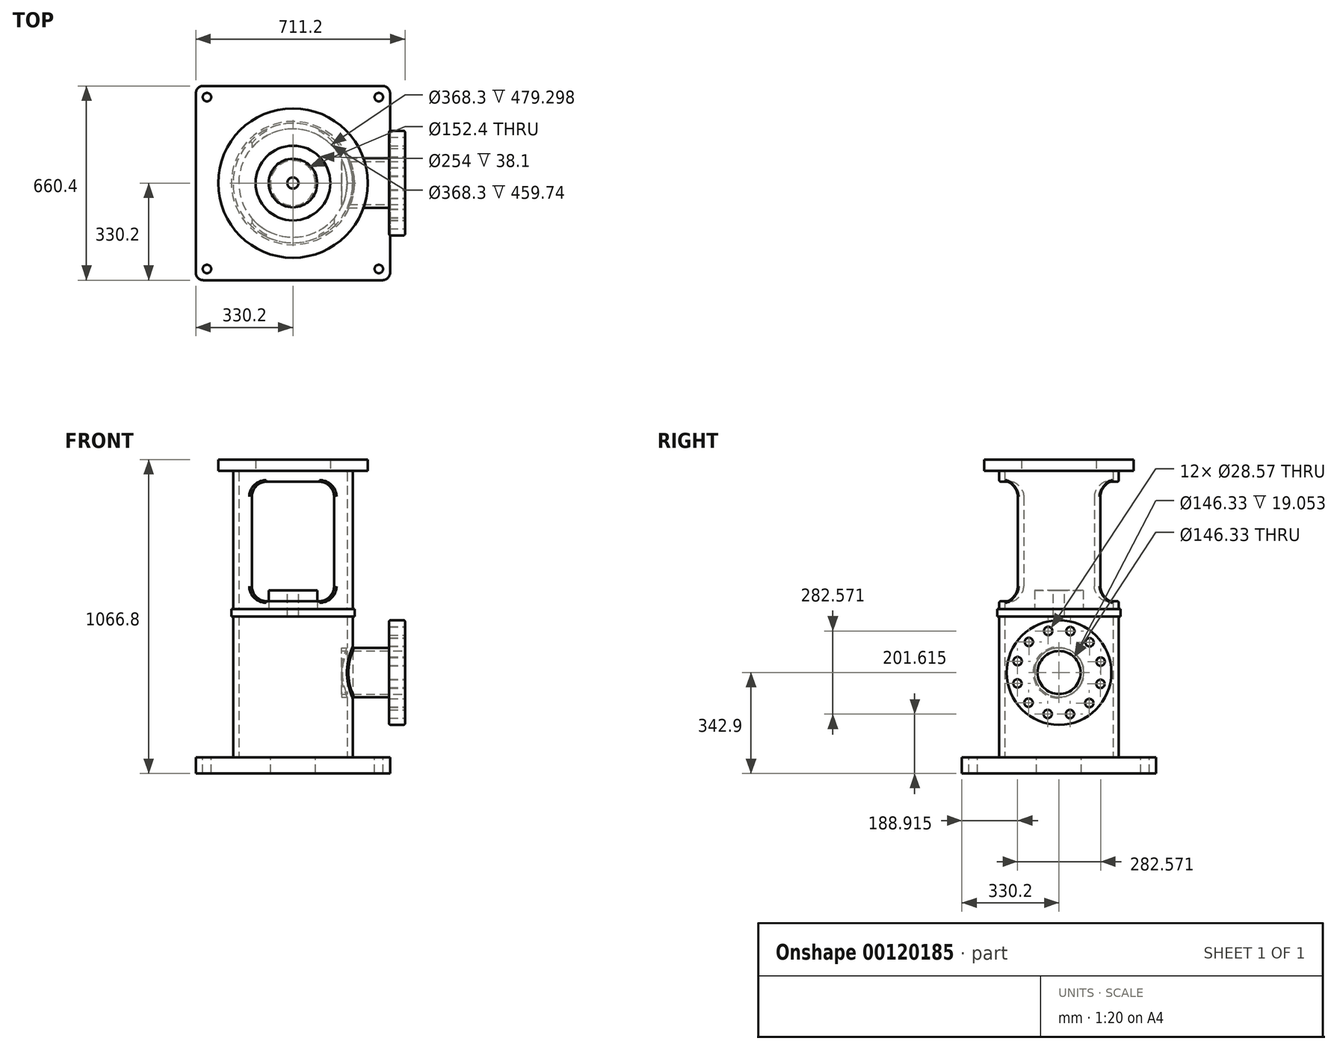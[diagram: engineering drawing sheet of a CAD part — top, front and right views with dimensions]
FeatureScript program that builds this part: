
annotation { "Feature Type Name" : "Feature", "Feature Type Description" : "" }
export const myFeature = defineFeature(function(context is Context, id is Id, definition is map)
    precondition{}
    {
        {
            var Q0;
            Q0=qCreatedBy(makeId("Top.planeOp"),FACE);
            var sketch = newSketch(context, id + "F0", { "sketchPlane" : qUnion([Q0])});
            skLineSegment(sketch, "E0.bottom", {"start": v(330.2, 330.2) * mm, "end": v(-330.2, 330.2) * mm});
            skLineSegment(sketch, "E0.top", {"start": v(330.2, -330.2) * mm, "end": v(-330.2, -330.2) * mm});
            skLineSegment(sketch, "E0.left", {"start": v(330.2, 330.2) * mm, "end": v(330.2, -330.2) * mm});
            skLineSegment(sketch, "E0.right", {"start": v(-330.2, 330.2) * mm, "end": v(-330.2, -330.2) * mm});
            skPoint(sketch, "E0.middle", {"position": v(0, 0) * mm});
            skSolve(sketch);
        }
        {
            var Q0;
            Q0 = qSketchRegion(id + "F0", true);
            extrude(context, id + "F1", {"entities" : qUnion([Q0]), "depth" : 54.1 * mm});
        }
        {
            var Q0;
            Q0=makeQuery(id+"F1.opExtrude","CAP_FACE",FACE,{"disambiguationData":[OSD([sQuery(id+"F0.wireOp",EDGE,"E0.bottom"),sQuery(id+"F0.wireOp",EDGE,"E0.top"),sQuery(id+"F0.wireOp",EDGE,"E0.left"),sQuery(id+"F0.wireOp",EDGE,"E0.right")])],"isStart":false});
            var sketch = newSketch(context, id + "F2", { "sketchPlane" : qUnion([Q0])});
            skCircle(sketch, "E1", {"center": v(0, 0) * mm, "radius": 203.2 * mm});
            skCircle(sketch, "E2", {"center": v(0, 0) * mm, "radius": 184.15 * mm});
            skSolve(sketch);
        }
        {
            var Q0;
            Q0 = qSketchRegion(id + "F2", true);
            extrude(context, id + "F3", {"entities" : qUnion([Q0]), "operationType" : NewBodyOperationType.ADD, "depth" : 974.6 * mm});
        }
        {
            var Q0;
            Q0=makeQuery(id+"F3.opExtrude","CAP_FACE",FACE,{"disambiguationData":[OSD([sQuery(id+"F2.wireOp",EDGE,"E1"),sQuery(id+"F2.wireOp",EDGE,"E2")])],"isStart":false});
            var sketch = newSketch(context, id + "F4", { "sketchPlane" : qUnion([Q0])});
            skCircle(sketch, "E3", {"center": v(0, 0) * mm, "radius": 127 * mm});
            skCircle(sketch, "E4", {"center": v(0, 0) * mm, "radius": 254 * mm});
            skSolve(sketch);
        }
        {
            var Q0;
            Q0 = qSketchRegion(id + "F4", true);
            extrude(context, id + "F5", {"entities" : qUnion([Q0]), "operationType" : NewBodyOperationType.ADD, "depth" : 38.1 * mm});
        }
        {
            var Q0;
            {var subQ0=sQuery(id+"F0.wireOp",EDGE,"E0.right");var subQ1=sQuery(id+"F0.wireOp",EDGE,"E0.left");var subQ2=sQuery(id+"F0.wireOp",EDGE,"E0.top");var subQ3=sQuery(id+"F0.wireOp",EDGE,"E0.bottom");Q0=makeQuery(id+"F3.boolean.opBoolean","SPLIT",FACE,{"disambiguationData":[TD([makeQuery(id+"F1.opExtrude","SWEPT_FACE",FACE,{"disambiguationData":[OSD([subQ3])]})])],"derivedFrom":makeQuery(id+"F1.opExtrude","CAP_FACE",FACE,{"disambiguationData":[OSD([subQ3,subQ2,subQ1,subQ0])],"isStart":false})});}
            var sketch = newSketch(context, id + "F6", { "sketchPlane" : qUnion([Q0])});
            skPoint(sketch, "E5.middle", {"position": v(0, 0) * mm});
            skCircle(sketch, "E6", {"center": v(292.1, -292.1) * mm, "radius": 14.35 * mm});
            skCircle(sketch, "E7", {"center": v(-292.1, -292.1) * mm, "radius": 14.35 * mm});
            skCircle(sketch, "E8", {"center": v(292.1, 292.1) * mm, "radius": 14.35 * mm});
            skCircle(sketch, "E9", {"center": v(-292.1, 292.1) * mm, "radius": 14.35 * mm});
            skSolve(sketch);
        }
        {
            var Q0;
            Q0 = qSketchRegion(id + "F6", true);
            extrude(context, id + "F7", {"entities" : qUnion([Q0]), "operationType" : NewBodyOperationType.REMOVE, "endBound" : BoundingType.THROUGH_ALL, "oppositeDirection" : true, "depth" : 25.4 * mm});
        }
        {
            var Q0;
            Q0=makeQuery(id+"F1.opExtrude","SWEPT_EDGE",EDGE,{"disambiguationData":[OSD([sQuery(id+"F0.wireOp",EDGE,"E0.top"),sQuery(id+"F0.wireOp",EDGE,"E0.left")])]});
            var Q1;
            Q1=makeQuery(id+"F1.opExtrude","SWEPT_EDGE",EDGE,{"disambiguationData":[OSD([sQuery(id+"F0.wireOp",EDGE,"E0.top"),sQuery(id+"F0.wireOp",EDGE,"E0.right")])]});
            var Q2;
            Q2=makeQuery(id+"F1.opExtrude","SWEPT_EDGE",EDGE,{"disambiguationData":[OSD([sQuery(id+"F0.wireOp",EDGE,"E0.bottom"),sQuery(id+"F0.wireOp",EDGE,"E0.right")])]});
            var Q3;
            Q3=makeQuery(id+"F1.opExtrude","SWEPT_EDGE",EDGE,{"disambiguationData":[OSD([sQuery(id+"F0.wireOp",EDGE,"E0.bottom"),sQuery(id+"F0.wireOp",EDGE,"E0.left")])]});
            fillet(context, id + "F8", {"entities" : qUnion([Q0, Q1, Q2, Q3]), "radius" : 25.4 * mm, "tangentPropagation" : true, "allowEdgeOverflow" : false});
        }
        {
            var Q0;
            {var subQ0=sQuery(id+"F0.wireOp",EDGE,"E0.right");var subQ1=sQuery(id+"F0.wireOp",EDGE,"E0.left");var subQ2=sQuery(id+"F0.wireOp",EDGE,"E0.top");var subQ3=sQuery(id+"F0.wireOp",EDGE,"E0.bottom");Q0=makeQuery(id+"F3.boolean.opBoolean","SPLIT",FACE,{"disambiguationData":[TD([makeQuery(id+"F1.opExtrude","SWEPT_FACE",FACE,{"disambiguationData":[OSD([subQ3])]})])],"derivedFrom":makeQuery(id+"F1.opExtrude","CAP_FACE",FACE,{"disambiguationData":[OSD([subQ3,subQ2,subQ1,subQ0])],"isStart":false})});}
            var sketch = newSketch(context, id + "F9", { "sketchPlane" : qUnion([Q0])});
            skCircle(sketch, "E10", {"center": v(0, 0) * mm, "radius": 76.2 * mm});
            skSolve(sketch);
        }
        {
            var Q0;
            Q0 = qSketchRegion(id + "F9", true);
            extrude(context, id + "F10", {"entities" : qUnion([Q0]), "operationType" : NewBodyOperationType.REMOVE, "endBound" : BoundingType.THROUGH_ALL, "oppositeDirection" : true, "depth" : 25.4 * mm});
        }
        {
            var Q0;
            Q0=makeQuery(id+"F1.opExtrude","SWEPT_FACE",FACE,{"disambiguationData":[OSD([sQuery(id+"F0.wireOp",EDGE,"E0.left")])]});
            var sketch = newSketch(context, id + "F11", { "sketchPlane" : qUnion([Q0])});
            skLineSegment(sketch, "E11", {"start": v(0, 0) * mm, "end": v(0, 804.54) * mm});
            skPoint(sketch, "E11.endSnap0", {"position": v(0, 0) * mm});
            skLineSegment(sketch, "E12", {"start": v(0, 0) * mm, "end": v(0, 342.9) * mm});
            skLineSegment(sketch, "E13", {"start": v(0, 342.9) * mm, "end": v(336.21, 342.9) * mm});
            skCircle(sketch, "E14", {"center": v(0, 342.9) * mm, "radius": 84.14 * mm});
            skCircle(sketch, "E15", {"center": v(0, 342.9) * mm, "radius": 73.16 * mm});
            skSolve(sketch);
        }
        {
            var Q0;
            Q0 = qSketchRegion(id + "F11", true);
            extrude(context, id + "F12", {"entities" : qUnion([Q0]), "operationType" : NewBodyOperationType.ADD, "oppositeDirection" : true, "depth" : 165.1 * mm});
        }
        {
            var Q0;
            Q0=makeQuery(id+"F12.opExtrude","CAP_FACE",FACE,{"disambiguationData":[OSD([sQuery(id+"F11.wireOp",EDGE,"E14"),sQuery(id+"F11.wireOp",EDGE,"E15")])],"isStart":true});
            extrude(context, id + "F13", {"entities" : qUnion([Q0]), "operationType" : NewBodyOperationType.ADD, "depth" : 50.8 * mm});
        }
        {
            var Q0;
            Q0=makeQuery(id+"F13.opExtrude","CAP_FACE",FACE,{"disambiguationData":[OSD([sQuery(id+"F11.wireOp",EDGE,"E14"),sQuery(id+"F11.wireOp",EDGE,"E15")])],"isStart":false});
            var sketch = newSketch(context, id + "F14", { "sketchPlane" : qUnion([Q0])});
            skCircle(sketch, "E16", {"center": v(0, 342.9) * mm, "radius": 177.8 * mm});
            skCircle(sketch, "E17", {"center": v(0, 342.9) * mm, "radius": 73.16 * mm});
            skSolve(sketch);
        }
        {
            var Q0;
            Q0 = qSketchRegion(id + "F14", true);
            extrude(context, id + "F15", {"entities" : qUnion([Q0]), "operationType" : NewBodyOperationType.ADD, "oppositeDirection" : true, "depth" : 54.1 * mm});
        }
        {
            var Q0;
            Q0=makeQuery(id+"F15.boolean.opBoolean","MERGE",FACE,{"derivedFrom":[makeQuery(id+"F13.opExtrude","CAP_FACE",FACE,{"disambiguationData":[OSD([sQuery(id+"F11.wireOp",EDGE,"E14"),sQuery(id+"F11.wireOp",EDGE,"E15")])],"isStart":false}),makeQuery(id+"F15.opExtrude","CAP_FACE",FACE,{"disambiguationData":[OSD([sQuery(id+"F14.wireOp",EDGE,"E16"),sQuery(id+"F14.wireOp",EDGE,"E17")])],"isStart":true})]});
            var sketch = newSketch(context, id + "F16", { "sketchPlane" : qUnion([Q0])});
            skPoint(sketch, "E18.center", {"position": v(0, 342.9) * mm});
            skCircle(sketch, "E19", {"center": v(38.6, 483.76) * mm, "radius": 14.29 * mm});
            skCircle(sketch, "E20.1.0", {"center": v(-37, 484.19) * mm, "radius": 14.29 * mm});
            skCircle(sketch, "E20.2.0", {"center": v(-102.69, 446.76) * mm, "radius": 14.29 * mm});
            skCircle(sketch, "E20.3.0", {"center": v(-140.86, 381.5) * mm, "radius": 14.29 * mm});
            skCircle(sketch, "E20.4.0", {"center": v(-141.29, 305.9) * mm, "radius": 14.29 * mm});
            skCircle(sketch, "E20.5.0", {"center": v(-103.86, 240.21) * mm, "radius": 14.29 * mm});
            skCircle(sketch, "E20.6.0", {"center": v(-38.6, 202.04) * mm, "radius": 14.29 * mm});
            skCircle(sketch, "E20.7.0", {"center": v(37, 201.61) * mm, "radius": 14.29 * mm});
            skCircle(sketch, "E20.8.0", {"center": v(102.69, 239.04) * mm, "radius": 14.29 * mm});
            skCircle(sketch, "E20.9.0", {"center": v(140.86, 304.3) * mm, "radius": 14.29 * mm});
            skCircle(sketch, "E20.10.0", {"center": v(141.29, 379.9) * mm, "radius": 14.29 * mm});
            skCircle(sketch, "E20.11.0", {"center": v(103.86, 445.59) * mm, "radius": 14.29 * mm});
            skSolve(sketch);
        }
        {
            var Q0;
            Q0 = qSketchRegion(id + "F16", true);
            extrude(context, id + "F17", {"entities" : qUnion([Q0]), "operationType" : NewBodyOperationType.REMOVE, "endBound" : BoundingType.UP_TO_NEXT, "oppositeDirection" : true, "depth" : 25.4 * mm});
        }
        {
            var Q0;
            Q0=makeQuery(id+"F15.opExtrude","CAP_EDGE",EDGE,{"disambiguationData":[OSD([sQuery(id+"F14.wireOp",EDGE,"E16")])],"isStart":true});
            var Q1;
            Q1=makeQuery(id+"F15.opExtrude","CAP_EDGE",EDGE,{"disambiguationData":[OSD([sQuery(id+"F14.wireOp",EDGE,"E16")])],"isStart":false});
            var Q2;
            {var subQ0=sQuery(id+"F11.wireOp",EDGE,"E14");Q2=makeQuery(id+"F15.boolean.opBoolean","INTERSECT",EDGE,{"derivedFrom":[makeQuery(id+"F13.boolean.opBoolean","MERGE",FACE,{"derivedFrom":[makeQuery(id+"F12.boolean.opBoolean","SPLIT",FACE,{"disambiguationData":[TD([makeQuery(id+"F3.opExtrude","SWEPT_FACE",FACE,{"disambiguationData":[OSD([sQuery(id+"F2.wireOp",EDGE,"E1")])]}),makeQuery(id+"F12.opExtrude","CAP_FACE",FACE,{"disambiguationData":[OSD([subQ0,sQuery(id+"F11.wireOp",EDGE,"E15")])],"isStart":true})])],"derivedFrom":makeQuery(id+"F12.opExtrude","SWEPT_FACE",FACE,{"disambiguationData":[OSD([subQ0])]})}),makeQuery(id+"F13.opExtrude","SWEPT_FACE",FACE,{"disambiguationData":[OSD([subQ0])]})]}),makeQuery(id+"F15.opExtrude","CAP_FACE",FACE,{"disambiguationData":[OSD([sQuery(id+"F14.wireOp",EDGE,"E16"),sQuery(id+"F14.wireOp",EDGE,"E17")])],"isStart":false})]});}
            var Q3;
            Q3=makeQuery(id+"F12.boolean.opBoolean","INTERSECT",EDGE,{"derivedFrom":[makeQuery(id+"F3.opExtrude","SWEPT_FACE",FACE,{"disambiguationData":[OSD([sQuery(id+"F2.wireOp",EDGE,"E1")])]}),makeQuery(id+"F12.opExtrude","SWEPT_FACE",FACE,{"disambiguationData":[OSD([sQuery(id+"F11.wireOp",EDGE,"E14")])]})]});
            fillet(context, id + "F18", {"entities" : qUnion([Q0, Q1, Q2, Q3]), "radius" : 5.08 * mm, "tangentPropagation" : true, "allowEdgeOverflow" : false});
        }
        {
            var Q0;
            Q0=makeQuery(id+"F1.opExtrude","SWEPT_FACE",FACE,{"disambiguationData":[OSD([sQuery(id+"F0.wireOp",EDGE,"E0.top")])]});
            var sketch = newSketch(context, id + "F19", { "sketchPlane" : qUnion([Q0])});
            skPoint(sketch, "E21.endSnap0", {"position": v(0, 0) * mm});
            skLineSegment(sketch, "E22.bottom", {"start": v(88.9, 991.73) * mm, "end": v(-88.9, 991.73) * mm});
            skLineSegment(sketch, "E22.top", {"start": v(88.9, 585.33) * mm, "end": v(-88.9, 585.33) * mm});
            skLineSegment(sketch, "E22.left", {"start": v(139.7, 940.93) * mm, "end": v(139.7, 636.13) * mm});
            skLineSegment(sketch, "E22.right", {"start": v(-139.7, 940.93) * mm, "end": v(-139.7, 636.13) * mm});
            skPoint(sketch, "E22.middle", {"position": v(0, 788.53) * mm});
            skPoint(sketch, "E23.visualSharp", {"position": v(-139.7, 991.73) * mm});
            skArc(sketch, "E23.filletArc", {"start": v(-88.9, 991.73) * mm, "mid": v(-124.82, 976.86) * mm, "end": v(-139.7, 940.93) * mm});
            skPoint(sketch, "E24.visualSharp", {"position": v(139.7, 991.73) * mm});
            skArc(sketch, "E24.filletArc", {"start": v(139.7, 940.93) * mm, "mid": v(124.82, 976.86) * mm, "end": v(88.9, 991.73) * mm});
            skPoint(sketch, "E25.visualSharp", {"position": v(139.7, 585.33) * mm});
            skArc(sketch, "E25.filletArc", {"start": v(88.9, 585.33) * mm, "mid": v(124.82, 600.21) * mm, "end": v(139.7, 636.13) * mm});
            skPoint(sketch, "E26.visualSharp", {"position": v(-139.7, 585.33) * mm});
            skArc(sketch, "E26.filletArc", {"start": v(-139.7, 636.13) * mm, "mid": v(-124.82, 600.21) * mm, "end": v(-88.9, 585.33) * mm});
            skSolve(sketch);
        }
        {
            var Q0;
            Q0 = qSketchRegion(id + "F19", true);
            extrude(context, id + "F20", {"entities" : qUnion([Q0]), "operationType" : NewBodyOperationType.REMOVE, "endBound" : BoundingType.THROUGH_ALL, "oppositeDirection" : true, "depth" : 25.4 * mm});
        }
        {
            var Q0;
            Q0=makeQuery(id+"F5.opExtrude","CAP_FACE",FACE,{"disambiguationData":[OSD([sQuery(id+"F4.wireOp",EDGE,"E3"),sQuery(id+"F4.wireOp",EDGE,"E4")])],"isStart":false});
            cPlane(context, id + "F21", {"entities" : qUnion([Q0]), "cplaneType" : CPlaneType.OFFSET, "offset" : 533.4 * mm, "oppositeDirection" : true, "width" : 152.4 * mm, "height" : 152.4 * mm});
        }
        {
            var Q0;
            Q0=qCreatedBy(id+"F21.planeOp",FACE);
            var sketch = newSketch(context, id + "F22", { "sketchPlane" : qUnion([Q0])});
            skCircle(sketch, "E27", {"center": v(0, 0) * mm, "radius": 209.55 * mm});
            skSolve(sketch);
        }
        {
            var Q0;
            Q0 = qSketchRegion(id + "F22", true);
            extrude(context, id + "F23", {"entities" : qUnion([Q0]), "operationType" : NewBodyOperationType.ADD, "depth" : 25.4 * mm});
        }
        {
            var Q0;
            Q0=makeQuery(id+"F23.boolean.opBoolean","SPLIT",FACE,{"disambiguationData":[TD([makeQuery(id+"F3.opExtrude","SWEPT_FACE",FACE,{"disambiguationData":[OSD([sQuery(id+"F2.wireOp",EDGE,"E2")])]})])],"derivedFrom":makeQuery(id+"F23.opExtrude","CAP_FACE",FACE,{"disambiguationData":[OSD([sQuery(id+"F22.wireOp",EDGE,"E27")])],"isStart":false})});
            var sketch = newSketch(context, id + "F24", { "sketchPlane" : qUnion([Q0])});
            skCircle(sketch, "E28", {"center": v(0, 0) * mm, "radius": 82.55 * mm});
            skSolve(sketch);
        }
        {
            var Q0;
            Q0 = qSketchRegion(id + "F24", true);
            extrude(context, id + "F25", {"entities" : qUnion([Q0]), "operationType" : NewBodyOperationType.ADD, "depth" : 63.5 * mm});
        }
        {
            var Q0;
            Q0=makeQuery(id+"F25.opExtrude","CAP_FACE",FACE,{"disambiguationData":[OSD([sQuery(id+"F24.wireOp",EDGE,"E28")])],"isStart":false});
            var sketch = newSketch(context, id + "F26", { "sketchPlane" : qUnion([Q0])});
            skCircle(sketch, "E29", {"center": v(0, 0) * mm, "radius": 19.05 * mm});
            skSolve(sketch);
        }
        {
            var Q0;
            Q0 = qSketchRegion(id + "F26", true);
            extrude(context, id + "F27", {"entities" : qUnion([Q0]), "operationType" : NewBodyOperationType.REMOVE, "endBound" : BoundingType.THROUGH_ALL, "oppositeDirection" : true, "depth" : 25.4 * mm});
        }
        {
            var Q0;
            Q0=makeQuery(id+"F3.opExtrude","CAP_EDGE",EDGE,{"disambiguationData":[OSD([sQuery(id+"F2.wireOp",EDGE,"E1")])],"isStart":true});
            var Q1;
            {var subQ0=sQuery(id+"F11.wireOp",EDGE,"E14");Q1=makeQuery(id+"F23.boolean.opBoolean","INTERSECT",EDGE,{"derivedFrom":[makeQuery(id+"F12.boolean.opBoolean","SPLIT",FACE,{"disambiguationData":[TD([makeQuery(id+"F12.opExtrude","SWEPT_FACE",FACE,{"disambiguationData":[OSD([subQ0])]})])],"derivedFrom":makeQuery(id+"F3.opExtrude","SWEPT_FACE",FACE,{"disambiguationData":[OSD([sQuery(id+"F2.wireOp",EDGE,"E2")])]})}),makeQuery(id+"F23.opExtrude","CAP_FACE",FACE,{"disambiguationData":[OSD([sQuery(id+"F22.wireOp",EDGE,"E27")])],"isStart":false})]});}
            var Q2;
            Q2=makeQuery(id+"F3.opExtrude","CAP_EDGE",EDGE,{"disambiguationData":[OSD([sQuery(id+"F2.wireOp",EDGE,"E1")])],"isStart":false});
            var Q3;
            Q3=makeQuery(id+"F3.opExtrude","CAP_EDGE",EDGE,{"disambiguationData":[OSD([sQuery(id+"F2.wireOp",EDGE,"E2")])],"isStart":false});
            fillet(context, id + "F28", {"entities" : qUnion([Q0, Q1, Q2, Q3]), "radius" : 5.08 * mm, "tangentPropagation" : true, "allowEdgeOverflow" : false});
        }
        {
            var Q0;
            Q0=makeQuery(id+"F20.boolean.opBoolean","INTERSECT",EDGE,{"disambiguationData":[OD(0.0)],"derivedFrom":[makeQuery(id+"F12.boolean.opBoolean","SPLIT",FACE,{"disambiguationData":[TD([makeQuery(id+"F12.opExtrude","SWEPT_FACE",FACE,{"disambiguationData":[OSD([sQuery(id+"F11.wireOp",EDGE,"E14")])]})])],"derivedFrom":makeQuery(id+"F3.opExtrude","SWEPT_FACE",FACE,{"disambiguationData":[OSD([sQuery(id+"F2.wireOp",EDGE,"E1")])]})}),makeQuery(id+"F20.opExtrude","SWEPT_FACE",FACE,{"disambiguationData":[OSD([sQuery(id+"F19.wireOp",EDGE,"E22.left")])]})]});
            var Q1;
            Q1=makeQuery(id+"F20.boolean.opBoolean","INTERSECT",EDGE,{"disambiguationData":[OD(1.0)],"derivedFrom":[makeQuery(id+"F12.boolean.opBoolean","SPLIT",FACE,{"disambiguationData":[TD([makeQuery(id+"F12.opExtrude","SWEPT_FACE",FACE,{"disambiguationData":[OSD([sQuery(id+"F11.wireOp",EDGE,"E14")])]})])],"derivedFrom":makeQuery(id+"F3.opExtrude","SWEPT_FACE",FACE,{"disambiguationData":[OSD([sQuery(id+"F2.wireOp",EDGE,"E1")])]})}),makeQuery(id+"F20.opExtrude","SWEPT_FACE",FACE,{"disambiguationData":[OSD([sQuery(id+"F19.wireOp",EDGE,"E22.right")])]})]});
            fillet(context, id + "F29", {"entities" : qUnion([Q0, Q1]), "radius" : 5.08 * mm, "tangentPropagation" : true, "allowEdgeOverflow" : false});
        }
    });
